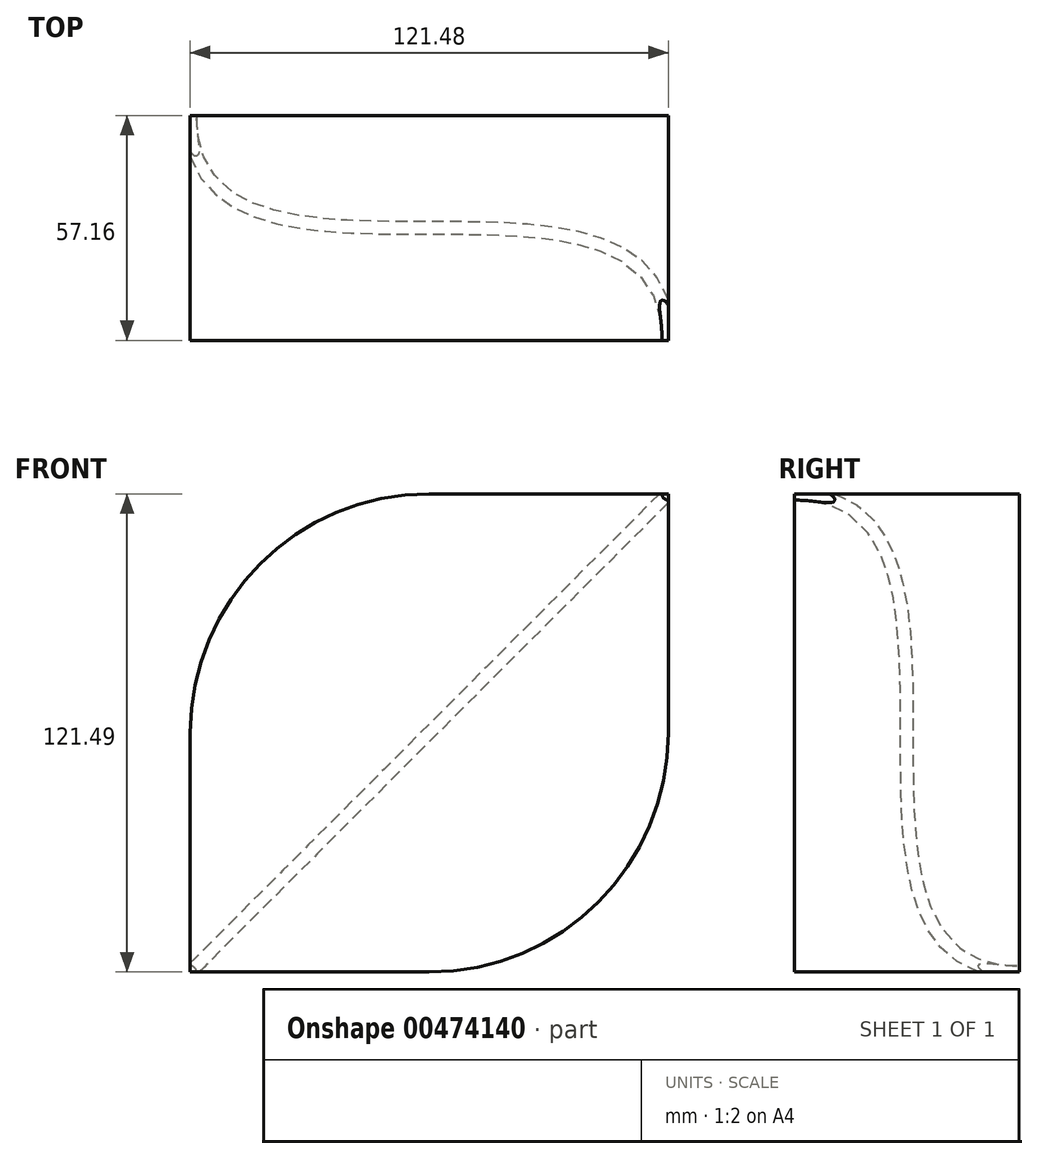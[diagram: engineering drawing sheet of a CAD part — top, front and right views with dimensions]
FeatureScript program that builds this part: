
annotation { "Feature Type Name" : "Feature", "Feature Type Description" : "" }
export const myFeature = defineFeature(function(context is Context, id is Id, definition is map)
    precondition{}
    {
        {
            var Q0;
            Q0=qCreatedBy(makeId("Front.planeOp"),FACE);
            var sketch = newSketch(context, id + "F0", { "sketchPlane" : qUnion([Q0])});
            skArc(sketch, "E0", {"start": v(0, 60.74) * mm, "mid": v(-42.95, 42.95) * mm, "end": v(-60.74, 0) * mm});
            skLineSegment(sketch, "E1.bottom", {"start": v(0, -60.74) * mm, "end": v(-60.74, -60.74) * mm});
            skLineSegment(sketch, "E1.top", {"start": v(60.74, 60.74) * mm, "end": v(0, 60.74) * mm});
            skLineSegment(sketch, "E1.left", {"start": v(60.74, 0) * mm, "end": v(60.74, 60.74) * mm});
            skLineSegment(sketch, "E1.right", {"start": v(-60.74, -60.74) * mm, "end": v(-60.74, 0) * mm});
            skPoint(sketch, "E2.orphan", {"position": v(-60.74, 60.74) * mm});
            skArc(sketch, "E3.trimOffspring", {"start": v(0, -60.74) * mm, "mid": v(42.95, -42.95) * mm, "end": v(60.74, 0) * mm});
            skPoint(sketch, "E4.orphan", {"position": v(60.74, -60.74) * mm});
            skSolve(sketch);
        }
        {
            var Q0;
            Q0 = qSketchRegion(id + "F0", true);
            extrude(context, id + "F1", {"entities" : qUnion([Q0]), "endBound" : BoundingType.SYMMETRIC, "depth" : 57.15 * mm});
        }
        {
            var Q0;
            Q0=makeQuery(id+"F1.opExtrude","CAP_VERTEX",VERTEX,{"disambiguationData":[OSD([sQuery(id+"F0.wireOp",EDGE,"E1.bottom"),sQuery(id+"F0.wireOp",EDGE,"E1.right")])],"isStart":false});
            var Q1;
            Q1=qCreatedBy(makeId("Origin.pointOp"),VERTEX);
            var Q2;
            Q2=makeQuery(id+"F1.opExtrude","CAP_VERTEX",VERTEX,{"disambiguationData":[OSD([sQuery(id+"F0.wireOp",EDGE,"E1.top"),sQuery(id+"F0.wireOp",EDGE,"E1.left")])],"isStart":false});
            cPlane(context, id + "F2", {"entities" : qUnion([Q0, Q1, Q2]), "cplaneType" : CPlaneType.THREE_POINT, "offset" : 25.4 * mm, "width" : 152.4 * mm, "height" : 152.4 * mm});
        }
        {
            var Q0;
            Q0=qCreatedBy(id+"F2.planeOp",FACE);
            var sketch = newSketch(context, id + "F3", { "sketchPlane" : qUnion([Q0])});
            skFitSpline(sketch, "E5", {"points": [v(-28.58, -85.9) * mm, v(0, 0) * mm, v(28.58, 85.9) * mm], "startDerivative": vector(172.2, 0) * mm, "endDerivative": vector(170.7, 0) * mm});
            skLineSegment(sketch, "E6", {"start": v(0, -85.9) * mm, "end": v(0, 85.9) * mm, "construction": true});
            skSolve(sketch);
        }
        {
            var Q0;
            Q0=makeQuery(id+"F1.opExtrude","CAP_FACE",FACE,{"disambiguationData":[OSD([sQuery(id+"F0.wireOp",EDGE,"E0"),sQuery(id+"F0.wireOp",EDGE,"E1.bottom"),sQuery(id+"F0.wireOp",EDGE,"E1.top"),sQuery(id+"F0.wireOp",EDGE,"E1.left"),sQuery(id+"F0.wireOp",EDGE,"E1.right"),sQuery(id+"F0.wireOp",EDGE,"E3.trimOffspring")])],"isStart":false});
            var sketch = newSketch(context, id + "F4", { "sketchPlane" : qUnion([Q0])});
            skCircle(sketch, "E7", {"center": v(60.74, 60.74) * mm, "radius": 1.59 * mm});
            skSolve(sketch);
        }
        {
            var Q0;
            Q0 = qSketchRegion(id + "F4", true);
            var Q1;
            Q1 = qConstructionFilter(qBodyType(qCreatedBy(id + "F3" ,EDGE), BodyType.WIRE), ConstructionObject.NO);
            sweep(context, id + "F5", {"operationType" : NewBodyOperationType.REMOVE, "profiles" : qUnion([Q0]), "path" : qUnion([Q1])});
        }
    });
